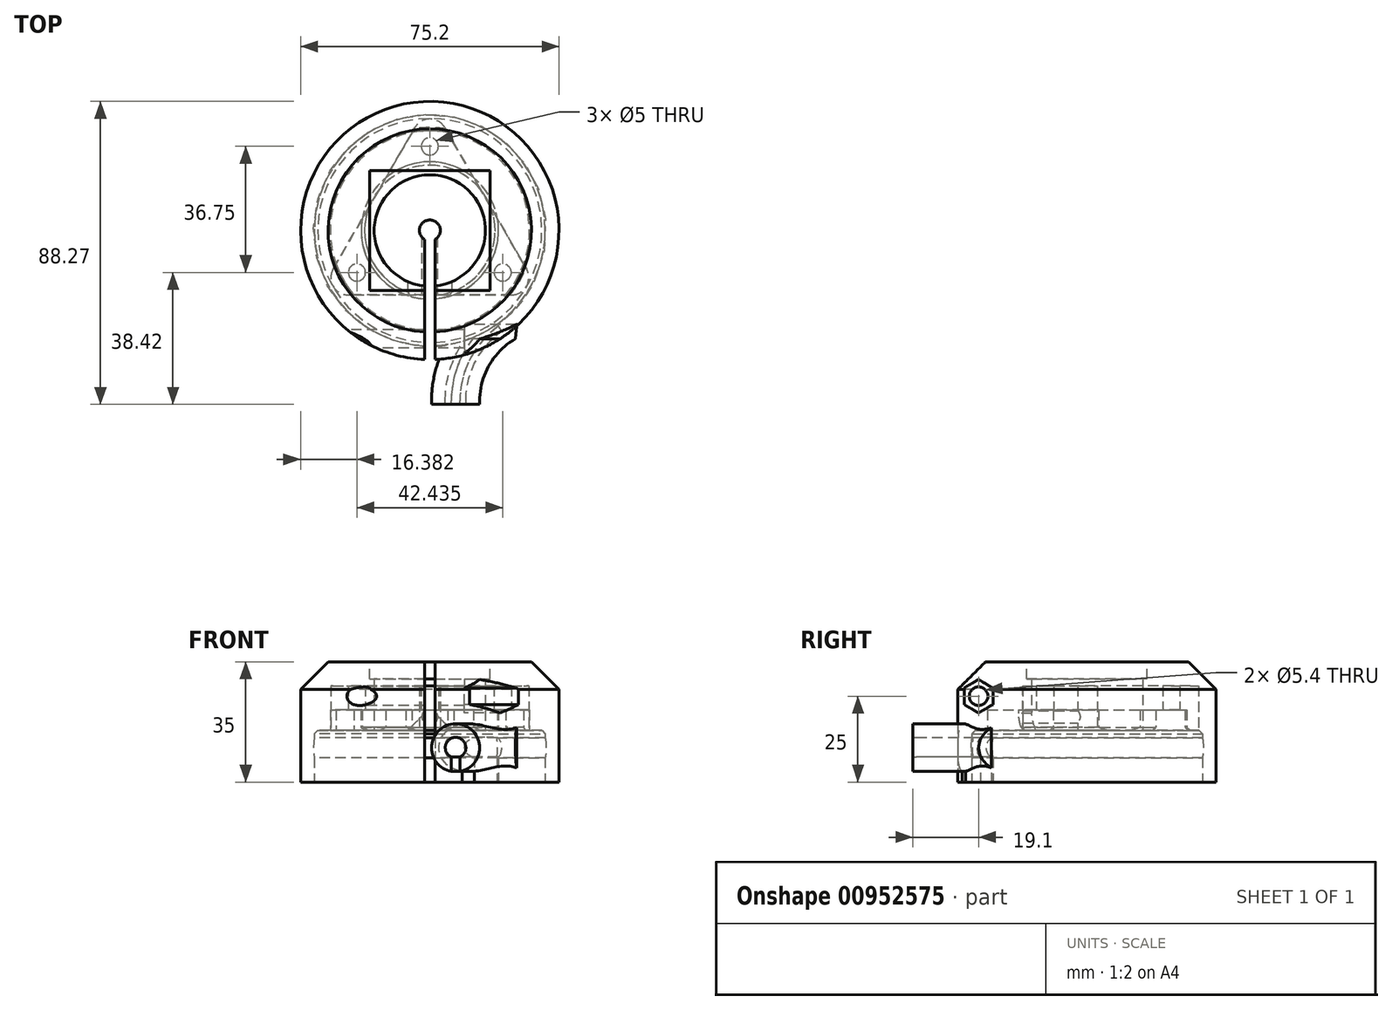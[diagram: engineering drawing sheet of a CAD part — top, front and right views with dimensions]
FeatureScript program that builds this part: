
annotation { "Feature Type Name" : "Feature", "Feature Type Description" : "" }
export const myFeature = defineFeature(function(context is Context, id is Id, definition is map)
    precondition{}
    {
        {
            var Q0;
            Q0=qCreatedBy(makeId("Top.planeOp"),FACE);
            var sketch = newSketch(context, id + "F0", { "sketchPlane" : qUnion([Q0])});
            skCircle(sketch, "E0", {"center": v(0, 0) * mm, "radius": 3.05 * mm});
            skCircle(sketch, "E1", {"center": v(0, 0) * mm, "radius": 13 * mm, "construction": true});
            skCircle(sketch, "E2", {"center": v(0, 0) * mm, "radius": 16 * mm});
            skLineSegment(sketch, "E3.bottom", {"start": v(-9.2, 9.2) * mm, "end": v(9.2, 9.2) * mm, "construction": true});
            skLineSegment(sketch, "E3.top", {"start": v(-9.2, -9.2) * mm, "end": v(9.2, -9.2) * mm, "construction": true});
            skLineSegment(sketch, "E3.left", {"start": v(-9.2, 9.2) * mm, "end": v(-9.2, -9.2) * mm, "construction": true});
            skLineSegment(sketch, "E3.right", {"start": v(9.2, 9.2) * mm, "end": v(9.2, -9.2) * mm, "construction": true});
            skCircle(sketch, "E4", {"center": v(9.2, 9.2) * mm, "radius": 1.7 * mm});
            skCircle(sketch, "E5", {"center": v(-9.2, 9.2) * mm, "radius": 1.7 * mm});
            skCircle(sketch, "E6", {"center": v(-9.2, -9.2) * mm, "radius": 1.7 * mm});
            skCircle(sketch, "E7", {"center": v(9.2, -9.2) * mm, "radius": 1.7 * mm});
            skCircle(sketch, "E8", {"center": v(0, 24.5) * mm, "radius": 8 * mm});
            skCircle(sketch, "E9", {"center": v(0, 24.5) * mm, "radius": 2.5 * mm});
            skLineSegment(sketch, "E10", {"start": v(0, 16.5) * mm, "end": v(0, 16) * mm, "construction": true});
            skCircle(sketch, "E11.cCircle", {"center": v(0, 0) * mm, "radius": 12.25 * mm, "construction": true});
            skLineSegment(sketch, "E11.0", {"start": v(0, 24.5) * mm, "end": v(21.22, -12.25) * mm, "construction": true});
            skLineSegment(sketch, "E11.1", {"start": v(21.22, -12.25) * mm, "end": v(-21.22, -12.25) * mm, "construction": true});
            skLineSegment(sketch, "E11.2", {"start": v(-21.22, -12.25) * mm, "end": v(0, 24.5) * mm, "construction": true});
            skPoint(sketch, "E11.0.midPoint", {"position": v(10.6, 6.12) * mm});
            skLineSegment(sketch, "E12.bottom", {"start": v(-17.5, 17.5) * mm, "end": v(17.5, 17.5) * mm});
            skLineSegment(sketch, "E12.top", {"start": v(-17.5, -17.5) * mm, "end": v(17.5, -17.5) * mm});
            skLineSegment(sketch, "E12.left", {"start": v(-17.5, 17.5) * mm, "end": v(-17.5, -17.5) * mm});
            skLineSegment(sketch, "E12.right", {"start": v(17.5, 17.5) * mm, "end": v(17.5, -17.5) * mm});
            skLineSegment(sketch, "E13", {"start": v(17.5, 17.5) * mm, "end": v(-17.5, -17.5) * mm, "construction": true});
            skLineSegment(sketch, "E14", {"start": v(0, 32.5) * mm, "end": v(0, 33.6) * mm, "construction": true});
            skCircle(sketch, "E15", {"center": v(0, 0) * mm, "radius": 32.5 * mm, "construction": true});
            skLineSegment(sketch, "E16", {"start": v(32.5, 0) * mm, "end": v(33.6, 0) * mm, "construction": true});
            skArc(sketch, "E17", {"start": v(33.6, 0) * mm, "mid": v(23.76, 23.76) * mm, "end": v(0, 33.6) * mm, "construction": true});
            skSolve(sketch);
        }
        {
            var Q0;
            Q0=qCreatedBy(makeId("Top.planeOp"),FACE);
            var sketch = newSketch(context, id + "F1", { "sketchPlane" : qUnion([Q0])});
            skCircle(sketch, "E18", {"center": v(0, 24.5) * mm, "radius": 2.5 * mm});
            skCircle(sketch, "E19", {"center": v(21.22, -12.25) * mm, "radius": 2.5 * mm});
            skCircle(sketch, "E20", {"center": v(-21.22, -12.25) * mm, "radius": 2.5 * mm});
            skCircle(sketch, "E21.cCircle", {"center": v(0, 0) * mm, "radius": 18.75 * mm, "construction": true});
            skLineSegment(sketch, "E21.0", {"start": v(0, 37.5) * mm, "end": v(32.48, -18.75) * mm});
            skLineSegment(sketch, "E21.1", {"start": v(32.48, -18.75) * mm, "end": v(-32.48, -18.75) * mm});
            skLineSegment(sketch, "E21.2", {"start": v(-32.48, -18.75) * mm, "end": v(0, 37.5) * mm});
            skPoint(sketch, "E21.0.midPoint", {"position": v(16.24, 9.37) * mm});
            skLineSegment(sketch, "E22", {"start": v(-21.22, -12.25) * mm, "end": v(-32.48, -18.75) * mm, "construction": true});
            skLineSegment(sketch, "E23", {"start": v(16.24, 9.37) * mm, "end": v(0, 0) * mm, "construction": true});
            skCircle(sketch, "E24", {"center": v(0, 0) * mm, "radius": 3.05 * mm});
            skSolve(sketch);
        }
        {
            var Q0;
            Q0=qSketchRegion(id+"F1",true);
            extrude(context, id + "F2", {"entities" : qUnion([Q0]), "depth" : 18 * mm});
        }
        {
            var Q0;
            Q0=qCreatedBy(makeId("Front.planeOp"),FACE);
            var sketch = newSketch(context, id + "F3", { "sketchPlane" : qUnion([Q0])});
            skLineSegment(sketch, "E25", {"start": v(-32.48, 18) * mm, "end": v(32.48, 0) * mm, "construction": true});
            skCircle(sketch, "E26", {"center": v(0, 9) * mm, "radius": 2.3 * mm});
            skSolve(sketch);
        }
        {
            var Q0;
            Q0=qSketchRegion(id+"F3",true);
            extrude(context, id + "F4", {"entities" : qUnion([Q0]), "operationType" : NewBodyOperationType.REMOVE, "endBound" : BoundingType.THROUGH_ALL, "depth" : 25 * mm});
        }
        {
            var Q0;
            Q0=qCreatedBy(makeId("Top.planeOp"),FACE);
            var sketch = newSketch(context, id + "F5", { "sketchPlane" : qUnion([Q0])});
            skCircle(sketch, "E27", {"center": v(0, 24.5) * mm, "radius": 2.5 * mm});
            skCircle(sketch, "E28", {"center": v(21.22, -12.25) * mm, "radius": 2.5 * mm});
            skCircle(sketch, "E29", {"center": v(-21.22, -12.25) * mm, "radius": 2.5 * mm});
            skCircle(sketch, "E30", {"center": v(0, 24.5) * mm, "radius": 4 * mm});
            skCircle(sketch, "E31", {"center": v(-21.22, -12.25) * mm, "radius": 4 * mm});
            skCircle(sketch, "E32", {"center": v(21.22, -12.25) * mm, "radius": 4 * mm});
            skSolve(sketch);
        }
        {
            var Q0;
            Q0=qSketchRegion(id+"F5",true);
            extrude(context, id + "F6", {"entities" : qUnion([Q0]), "operationType" : NewBodyOperationType.ADD, "oppositeDirection" : true, "depth" : 2 * mm});
        }
        {
            var Q0;
            Q0=makeQuery(id+"F6.opExtrude","CAP_EDGE",EDGE,{"disambiguationData":[OSD([sQuery(id+"F5.wireOp",EDGE,"E31")])],"isStart":false});
            var Q1;
            Q1=makeQuery(id+"F6.opExtrude","CAP_EDGE",EDGE,{"disambiguationData":[OSD([sQuery(id+"F5.wireOp",EDGE,"E32")])],"isStart":false});
            var Q2;
            Q2=makeQuery(id+"F6.opExtrude","CAP_EDGE",EDGE,{"disambiguationData":[OSD([sQuery(id+"F5.wireOp",EDGE,"E30")])],"isStart":false});
            chamfer(context, id + "F7", {"entities" : qUnion([Q0, Q1, Q2]), "width" : 1 * mm, "tangentPropagation" : true});
        }
        {
            var Q0;
            Q0=qCreatedBy(makeId("Top.planeOp"),FACE);
            var sketch = newSketch(context, id + "F8", { "sketchPlane" : qUnion([Q0])});
            skCircle(sketch, "E33", {"center": v(0, 0) * mm, "radius": 10 * mm});
            skSolve(sketch);
        }
        {
            var Q0;
            Q0=qSketchRegion(id+"F8",true);
            extrude(context, id + "F9", {"entities" : qUnion([Q0]), "operationType" : NewBodyOperationType.REMOVE, "depth" : 3 * mm});
        }
        {
            var Q0;
            Q0=makeQuery(id+"F2.opExtrude","SWEPT_EDGE",EDGE,{"disambiguationData":[OSD([sQuery(id+"F1.wireOp",EDGE,"E21.1"),sQuery(id+"F1.wireOp",EDGE,"E21.2")])]});
            var Q1;
            Q1=makeQuery(id+"F2.opExtrude","SWEPT_EDGE",EDGE,{"disambiguationData":[OSD([sQuery(id+"F1.wireOp",EDGE,"E21.0"),sQuery(id+"F1.wireOp",EDGE,"E21.1")])]});
            var Q2;
            Q2=makeQuery(id+"F2.opExtrude","SWEPT_EDGE",EDGE,{"disambiguationData":[OSD([sQuery(id+"F1.wireOp",EDGE,"E21.0"),sQuery(id+"F1.wireOp",EDGE,"E21.2")])]});
            fillet(context, id + "F10", {"entities" : qUnion([Q0, Q1, Q2]), "radius" : 5 * mm, "tangentPropagation" : true, "allowEdgeOverflow" : false});
        }
        {
            var Q0;
            Q0=qCreatedBy(makeId("Top.planeOp"),FACE);
            var sketch = newSketch(context, id + "F11", { "sketchPlane" : qUnion([Q0])});
            skCircle(sketch, "E34.0", {"center": v(0, 0) * mm, "radius": 16.2 * mm});
            skCircle(sketch, "E35", {"center": v(0, 0) * mm, "radius": 37.6 * mm});
            skSolve(sketch);
        }
        {
            var Q0;
            Q0=qSketchRegion(id+"F11",true);
            extrude(context, id + "F12", {"entities" : qUnion([Q0]), "depth" : 25 * mm, "hasSecondDirection" : true, "secondDirectionOppositeDirection" : true, "secondDirectionDepth" : 10 * mm});
        }
        {
            var Q0;
            Q0=qCreatedBy(makeId("Front.planeOp"),FACE);
            var sketch = newSketch(context, id + "F13", { "sketchPlane" : qUnion([Q0])});
            skEllipse(sketch, "E36", {"center": v(33.05, 0) * mm, "majorRadius": 4 * mm, "minorRadius": 0.8 * mm, "majorAxis": v(0, 1)});
            skLineSegment(sketch, "E37", {"start": v(0, 0) * mm, "end": v(0, 9.45) * mm, "construction": true});
            skSolve(sketch);
        }
        {
            var Q0;
            Q0=qSketchRegion(id+"F13",true);
            var Q1;
            Q1=sQuery(id+"F13.wireOp",EDGE,"E37");
            revolve(context, id + "F14", {"operationType" : NewBodyOperationType.REMOVE, "entities" : qUnion([Q0]), "axis" : qUnion([Q1]), "revolveType" : RevolveType.FULL, "oppositeDirection" : true});
        }
        {
            var Q0;
            Q0=makeQuery(id+"F12.opExtrude","CAP_FACE",FACE,{"disambiguationData":[OSD([sQuery(id+"F11.wireOp",EDGE,"E34.0"),sQuery(id+"F11.wireOp",EDGE,"E35")])],"isStart":true});
            var sketch = newSketch(context, id + "F15", { "sketchPlane" : qUnion([Q0])});
            skCircle(sketch, "E38", {"center": v(0, 0) * mm, "radius": 33.6 * mm});
            skSolve(sketch);
        }
        {
            var Q0;
            Q0=makeQuery(id+"F12.opExtrude","CAP_FACE",FACE,{"disambiguationData":[OSD([sQuery(id+"F11.wireOp",EDGE,"E34.0"),sQuery(id+"F11.wireOp",EDGE,"E35")])],"isStart":false});
            var sketch = newSketch(context, id + "F16", { "sketchPlane" : qUnion([Q0])});
            skLineSegment(sketch, "E39.bottom", {"start": v(-17.5, 17.5) * mm, "end": v(17.5, 17.5) * mm});
            skLineSegment(sketch, "E39.top", {"start": v(-17.5, -17.5) * mm, "end": v(17.5, -17.5) * mm});
            skLineSegment(sketch, "E39.left", {"start": v(-17.5, 17.5) * mm, "end": v(-17.5, -17.5) * mm});
            skLineSegment(sketch, "E39.right", {"start": v(17.5, 17.5) * mm, "end": v(17.5, -17.5) * mm});
            skSolve(sketch);
        }
        {
            var Q0;
            Q0=qSketchRegion(id+"F16",true);
            extrude(context, id + "F17", {"entities" : qUnion([Q0]), "operationType" : NewBodyOperationType.REMOVE, "oppositeDirection" : true, "depth" : 5 * mm});
        }
        {
            var Q0;
            Q0=qCreatedBy(makeId("Top.planeOp"),FACE);
            var sketch = newSketch(context, id + "F18", { "sketchPlane" : qUnion([Q0])});
            skLineSegment(sketch, "E40.bottom", {"start": v(1.5, 0) * mm, "end": v(-1.5, 0) * mm});
            skLineSegment(sketch, "E40.top", {"start": v(1.5, -46.22) * mm, "end": v(-1.5, -46.22) * mm});
            skLineSegment(sketch, "E40.left", {"start": v(-1.5, 0) * mm, "end": v(-1.5, -46.22) * mm});
            skLineSegment(sketch, "E40.right", {"start": v(1.5, 0) * mm, "end": v(1.5, -46.22) * mm});
            skSolve(sketch);
        }
        {
            var Q0;
            Q0=qSketchRegion(id+"F18",true);
            extrude(context, id + "F19", {"entities" : qUnion([Q0]), "operationType" : NewBodyOperationType.REMOVE, "endBound" : BoundingType.THROUGH_ALL, "depth" : 25 * mm, "hasSecondDirection" : true, "secondDirectionOppositeDirection" : true, "secondDirectionDepth" : 25 * mm});
        }
        {
            var Q0;
            Q0=sQuery(id+"F13.wireOp",VERTEX,"E36.center");
            var Q1;
            Q1=qCreatedBy(makeId("Top.planeOp"),FACE);
            cPlane(context, id + "F20", {"entities" : qUnion([Q0, Q1]), "cplaneType" : CPlaneType.PLANE_POINT, "offset" : 25 * mm, "width" : 150 * mm, "height" : 150 * mm});
        }
        {
            var Q0;
            Q0=qCreatedBy(id+"F20.planeOp",FACE);
            var sketch = newSketch(context, id + "F21", { "sketchPlane" : qUnion([Q0])});
            skArc(sketch, "E41", {"start": v(19.22, -26.89) * mm, "mid": v(29.39, -15.12) * mm, "end": v(33.05, 0) * mm, "construction": true});
            skArc(sketch, "E42", {"start": v(19.22, -26.89) * mm, "mid": v(10.6, -36.86) * mm, "end": v(7.5, -49.67) * mm});
            skLineSegment(sketch, "E43", {"start": v(7.5, -49.67) * mm, "end": v(7.5, -50.67) * mm});
            skLineSegment(sketch, "E44", {"start": v(10.5, -50.67) * mm, "end": v(4.5, -50.67) * mm, "construction": true});
            skSolve(sketch);
        }
        {
            var Q0;
            Q0=sQuery(id+"F21.wireOp",EDGE,"E44");
            var Q1;
            Q1=qCreatedBy(id+"F20.planeOp",FACE);
            cPlane(context, id + "F22", {"entities" : qUnion([Q0, Q1]), "cplaneType" : CPlaneType.LINE_ANGLE, "offset" : 25 * mm, "angle" : 90 * degree, "width" : 150 * mm, "height" : 150 * mm});
        }
        {
            var Q0;
            Q0=qCreatedBy(id+"F22.planeOp",FACE);
            var sketch = newSketch(context, id + "F23", { "sketchPlane" : qUnion([Q0])});
            skCircle(sketch, "E45", {"center": v(7.5, 0) * mm, "radius": 3 * mm});
            skCircle(sketch, "E46", {"center": v(7.5, 0) * mm, "radius": 7 * mm});
            skSolve(sketch);
        }
        {
            var Q0;
            Q0=makeQuery(id+"F23.imprint","IMPRINT",FACE,{"disambiguationData":[TD([[makeQuery(id+"F23.imprint","IMPRINT",EDGE,{"derivedFrom":sQuery(id+"F23.wireOp",EDGE,"E45")}),-1.0]])]});
            var Q1;
            Q1=qConstructionFilter(qBodyType(qCreatedBy(id+"F21",EDGE),BodyType.WIRE),ConstructionObject.NO);
            sweep(context, id + "F24", {"operationType" : NewBodyOperationType.ADD, "profiles" : qUnion([Q0]), "path" : qUnion([Q1])});
        }
        {
            var Q0;
            Q0=makeQuery(id+"F23.imprint","IMPRINT",FACE,{"disambiguationData":[TD([[makeQuery(id+"F23.imprint","IMPRINT",EDGE,{"derivedFrom":sQuery(id+"F23.wireOp",EDGE,"E45")}),1.0]])]});
            var Q1;
            Q1=qConstructionFilter(qBodyType(qCreatedBy(id+"F21",EDGE),BodyType.WIRE),ConstructionObject.NO);
            sweep(context, id + "F25", {"operationType" : NewBodyOperationType.REMOVE, "profiles" : qUnion([Q0]), "path" : qUnion([Q1])});
        }
        {
            var Q0;
            Q0=qCreatedBy(id+"F22.planeOp",FACE);
            var sketch = newSketch(context, id + "F26", { "sketchPlane" : qUnion([Q0])});
            skLineSegment(sketch, "E47.bottom", {"start": v(8.75, 0) * mm, "end": v(6.25, 0) * mm});
            skLineSegment(sketch, "E47.top", {"start": v(8.75, -35.68) * mm, "end": v(6.25, -35.68) * mm});
            skLineSegment(sketch, "E47.left", {"start": v(6.25, 0) * mm, "end": v(6.25, -35.68) * mm});
            skLineSegment(sketch, "E47.right", {"start": v(8.75, 0) * mm, "end": v(8.75, -35.68) * mm});
            skSolve(sketch);
        }
        {
            var Q0;
            Q0=qSketchRegion(id+"F26",true);
            var Q1;
            Q1=qConstructionFilter(qBodyType(qCreatedBy(id+"F21",EDGE),BodyType.WIRE),ConstructionObject.NO);
            sweep(context, id + "F27", {"operationType" : NewBodyOperationType.REMOVE, "profiles" : qUnion([Q0]), "path" : qUnion([Q1])});
        }
        {
            var Q0;
            Q0=qSketchRegion(id+"F15",true);
            extrude(context, id + "F28", {"entities" : qUnion([Q0]), "operationType" : NewBodyOperationType.REMOVE, "oppositeDirection" : true, "depth" : 15 * mm});
        }
        {
            var Q0;
            Q0=makeQuery(id+"F28.boolean.opBoolean","COPY",FACE,{"derivedFrom":makeQuery(id+"F28.opExtrude","CAP_FACE",FACE,{"disambiguationData":[OSD([sQuery(id+"F15.wireOp",EDGE,"E38")])],"isStart":false})});
            var sketch = newSketch(context, id + "F29", { "sketchPlane" : qUnion([Q0])});
            skCircle(sketch, "E48", {"center": v(0, 0) * mm, "radius": 20 * mm});
            skCircle(sketch, "E49", {"center": v(0, 0) * mm, "radius": 29 * mm});
            skCircle(sketch, "E50", {"center": v(0, -1.12) * mm, "radius": 23.38 * mm, "construction": true});
            skSolve(sketch);
        }
        {
            var Q0;
            Q0=qSketchRegion(id+"F29",true);
            extrude(context, id + "F30", {"entities" : qUnion([Q0]), "operationType" : NewBodyOperationType.REMOVE, "oppositeDirection" : true, "depth" : 6 * mm});
        }
        {
            var Q0;
            Q0=makeQuery(id+"F19.boolean.opBoolean","COPY",FACE,{"derivedFrom":makeQuery(id+"F19.opExtrude","SWEPT_FACE",FACE,{"disambiguationData":[OSD([sQuery(id+"F18.wireOp",EDGE,"E40.right")])]})});
            var sketch = newSketch(context, id + "F31", { "sketchPlane" : qUnion([Q0])});
            skLineSegment(sketch, "E51", {"start": v(28.96, 5) * mm, "end": v(37.57, 25) * mm, "construction": true});
            skCircle(sketch, "E52", {"center": v(31.57, 15) * mm, "radius": 2.7 * mm});
            skSolve(sketch);
        }
        {
            var Q0;
            Q0=qSketchRegion(id+"F31",true);
            extrude(context, id + "F32", {"entities" : qUnion([Q0]), "operationType" : NewBodyOperationType.REMOVE, "endBound" : BoundingType.THROUGH_ALL, "oppositeDirection" : true, "depth" : 25 * mm, "hasSecondDirection" : true, "secondDirectionBound" : SecondDirectionBoundingType.THROUGH_ALL, "secondDirectionOppositeDirection" : false, "secondDirectionDepth" : 25 * mm});
        }
        {
            var Q0;
            Q0=qCreatedBy(makeId("Right.planeOp"),FACE);
            cPlane(context, id + "F33", {"entities" : qUnion([Q0]), "cplaneType" : CPlaneType.OFFSET, "offset" : 10 * mm, "width" : 150 * mm, "height" : 150 * mm});
        }
        {
            var Q0;
            Q0=qCreatedBy(id+"F33.planeOp",FACE);
            var sketch = newSketch(context, id + "F34", { "sketchPlane" : qUnion([Q0])});
            skCircle(sketch, "E53.cCircle", {"center": v(-31.57, 15) * mm, "radius": 4.2 * mm, "construction": true});
            skLineSegment(sketch, "E53.0", {"start": v(-35.77, 12.58) * mm, "end": v(-35.77, 17.42) * mm});
            skLineSegment(sketch, "E53.1", {"start": v(-35.77, 17.42) * mm, "end": v(-31.57, 19.85) * mm});
            skLineSegment(sketch, "E53.2", {"start": v(-31.57, 19.85) * mm, "end": v(-27.37, 17.42) * mm});
            skLineSegment(sketch, "E53.3", {"start": v(-27.37, 17.42) * mm, "end": v(-27.37, 12.58) * mm});
            skLineSegment(sketch, "E53.4", {"start": v(-27.37, 12.58) * mm, "end": v(-31.57, 10.15) * mm});
            skLineSegment(sketch, "E53.5", {"start": v(-31.57, 10.15) * mm, "end": v(-35.77, 12.58) * mm});
            skPoint(sketch, "E53.0.midPoint", {"position": v(-35.77, 15) * mm});
            skSolve(sketch);
        }
        {
            var Q0;
            Q0=qSketchRegion(id+"F34",true);
            extrude(context, id + "F35", {"entities" : qUnion([Q0]), "operationType" : NewBodyOperationType.REMOVE, "endBound" : BoundingType.THROUGH_ALL, "depth" : 25 * mm});
        }
        {
            var Q0;
            Q0=makeQuery(id+"F12.opExtrude","CAP_EDGE",EDGE,{"disambiguationData":[OSD([sQuery(id+"F11.wireOp",EDGE,"E35")])],"isStart":false});
            chamfer(context, id + "F36", {"entities" : qUnion([Q0]), "width" : 8 * mm, "tangentPropagation" : true});
        }
        {
            var Q0;
            Q0=makeQuery(id+"F28.boolean.opBoolean","COPY",EDGE,{"derivedFrom":makeQuery(id+"F28.opExtrude","CAP_EDGE",EDGE,{"disambiguationData":[OSD([sQuery(id+"F15.wireOp",EDGE,"E38")])],"isStart":false})});
            var Q1;
            Q1=makeQuery(id+"F30.boolean.opBoolean","COPY",EDGE,{"derivedFrom":makeQuery(id+"F30.opExtrude","CAP_EDGE",EDGE,{"disambiguationData":[OSD([sQuery(id+"F29.wireOp",EDGE,"E49")])],"isStart":true})});
            var Q2;
            Q2=makeQuery(id+"F30.boolean.opBoolean","COPY",EDGE,{"derivedFrom":makeQuery(id+"F30.opExtrude","CAP_EDGE",EDGE,{"disambiguationData":[OSD([sQuery(id+"F29.wireOp",EDGE,"E48")])],"isStart":true})});
            chamfer(context, id + "F37", {"entities" : qUnion([Q0, Q1, Q2]), "width" : 1 * mm, "tangentPropagation" : true});
        }
        {
            var Q0;
            Q0=makeQuery(id+"F24.boolean.opBoolean","INTERSECT",EDGE,{"derivedFrom":[makeQuery(id+"F12.opExtrude","SWEPT_FACE",FACE,{"disambiguationData":[OSD([sQuery(id+"F11.wireOp",EDGE,"E35")])]}),makeQuery(id+"F24.opSweep","CAP_FACE",FACE,{"disambiguationData":[OSD([sQuery(id+"F21.wireOp",VERTEX,"E42.start"),sQuery(id+"F23.wireOp",EDGE,"E45"),sQuery(id+"F23.wireOp",EDGE,"E46")])],"isStart":false})]});
            var Q1;
            {var subQ0=sQuery(id+"F23.wireOp",EDGE,"E46");var subQ1=sQuery(id+"F23.wireOp",EDGE,"E45");var subQ2=sQuery(id+"F21.wireOp",VERTEX,"E42.start");var subQ3=sQuery(id+"F11.wireOp",EDGE,"E35");Q1=makeQuery(id+"F9cw4HUznN2mPc6_2.1.F24.boolean.opBoolean","INTERSECT",EDGE,{"derivedFrom":[makeQuery(id+"F24.boolean.opBoolean","SPLIT",FACE,{"disambiguationData":[TD([makeQuery(id+"F19.boolean.opBoolean","COPY",FACE,{"derivedFrom":makeQuery(id+"F19.opExtrude","SWEPT_FACE",FACE,{"disambiguationData":[OSD([sQuery(id+"F18.wireOp",EDGE,"E40.left")])]})})])],"derivedFrom":makeQuery(id+"F12.opExtrude","SWEPT_FACE",FACE,{"disambiguationData":[OSD([subQ3])]})}),makeQuery(id+"F9cw4HUznN2mPc6_2.1.F24.opSweep","CAP_FACE",FACE,{"disambiguationData":[OSD([subQ2,subQ1,subQ0])],"isStart":false})]});}
            var Q2;
            {var subQ0=makeQuery(id+"F19.boolean.opBoolean","COPY",FACE,{"derivedFrom":makeQuery(id+"F19.opExtrude","SWEPT_FACE",FACE,{"disambiguationData":[OSD([sQuery(id+"F18.wireOp",EDGE,"E40.right")])]})});var subQ1=makeQuery(id+"F28.opExtrude","CAP_FACE",FACE,{"disambiguationData":[OSD([sQuery(id+"F15.wireOp",EDGE,"E38")])],"isStart":false});Q2=makeQuery(id+"F30.boolean.opBoolean","SPLIT",EDGE,{"disambiguationData":[TD([makeQuery(id+"F12.opExtrude","SWEPT_FACE",FACE,{"disambiguationData":[OSD([sQuery(id+"F11.wireOp",EDGE,"E34.0")])]})])],"derivedFrom":makeQuery(id+"F28.boolean.opBoolean","INTERSECT",EDGE,{"derivedFrom":[subQ0,subQ1]})});}
            var Q3;
            {var subQ0=makeQuery(id+"F19.boolean.opBoolean","COPY",FACE,{"derivedFrom":makeQuery(id+"F19.opExtrude","SWEPT_FACE",FACE,{"disambiguationData":[OSD([sQuery(id+"F18.wireOp",EDGE,"E40.left")])]})});var subQ1=makeQuery(id+"F28.opExtrude","CAP_FACE",FACE,{"disambiguationData":[OSD([sQuery(id+"F15.wireOp",EDGE,"E38")])],"isStart":false});Q3=makeQuery(id+"F30.boolean.opBoolean","SPLIT",EDGE,{"disambiguationData":[TD([makeQuery(id+"F12.opExtrude","SWEPT_FACE",FACE,{"disambiguationData":[OSD([sQuery(id+"F11.wireOp",EDGE,"E34.0")])]})])],"derivedFrom":makeQuery(id+"F28.boolean.opBoolean","INTERSECT",EDGE,{"derivedFrom":[subQ0,subQ1]})});}
            chamfer(context, id + "F38", {"entities" : qUnion([Q0, Q1, Q2, Q3]), "width" : 5 * mm, "tangentPropagation" : true});
        }
    });
